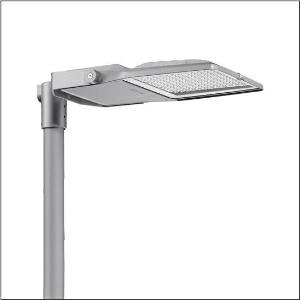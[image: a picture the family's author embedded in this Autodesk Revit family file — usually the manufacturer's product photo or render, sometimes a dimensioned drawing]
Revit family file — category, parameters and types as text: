
# Revit family: floodlight_fl_21_iq_midi___pl61_5xa7782f2c3a_b633
name_source: partatom
category: Lighting Fixtures
units: mm (PartAtom-declared; Revit-internal decimal feet)

## family parameters
Cut with Voids When Loaded = No
Host = Face
Light Source = No
Part Type = Normal
Room Calculation Point = No
Round Connector Dimension = Use Diameter
Shared = No

## types (1)
- --- (1 x LED, 35100 lm, 270.2 W, 3000K)
    Apparent Load = 270 VA
    CIE Flux Codes = 33 65 98 100 100
    Color Rendering = 70
    Color Temperature = 3000K
    Default Elevation = 1800 mm
    Description = Floodlight FL 21 iQ midi, floodlight, primary light control with lens, of PMMA, primary optical cover: protective disc, of toughened safety glass, transparent, light distribution: PL61, light emission: direct distribution, installation type: surface-mounted, lamps: LED, High Power LED, rated values: 35.100lm | 270,2W | 129,9lm/W (begin service life); end service life: 35.100lm | 286,6W; at 50% lumin. flux: 17.550lm | 117,4W | 149,5lm/W, colour temperature: 3000K, colour rendering: CRI > 70, light colour: 730, light setting 1 begin service life: 100% | 35.100lm | 270,2W | 129,9lm/W | 3.000K, light setting 1 end service life: 286,6W, further light settings possible, control: optimised constant luminous flux control (CLO 2.0), Desk-Remote (wireless, voltage-free reading and setting of iQ features in the workshop via application-optimized NFC function/RFID function), Smart-Wire, Night-Set, Temp-Guard, Auto-Match, Street-Remote, pre-setting: linear dimming characteristic, with terminal, 6-pole, mains connection: 220..240V, AC, 50/60Hz, luminaire housing, of diecast aluminium, powder-coated, SITECO metallic grey (DB 702S), corrosivity category C5 mid according to DIN EN ISO 12944suitable for swimming poolschlorine-resistant, sealing non-destructively replaceable, please order mast flange separately, mast bracket, of steel, galvanised, powder-coated, SITECO metallic grey (DB 702S), protection rating (complete): IP66, insulation class (complete): insulation class II (safety insulation), certification: CE, ENEC, VDE, protection symbol: D, impact resistance: IK08, permissible operating ambient temperature: -40..+40°C, permissible operating ambient temperature for outdoor applications: -40..+50°C, standard: DIN EN 12944, LABS conformity tested according to VDMA 24364:2018-05, packaging unit: 1 piece

Light Distribution: PL61
    Height = 76 mm
    Lamp = 1 x LED
    Lamp Light Flux = 35100 lm
    Lamp Power = 270.2 W
    Lamp count = 1
    Length = 657 mm
    Luminous efficacy = 130 lm/W
    Manufacturer = Siteco
    ModVariant = No
    Model = 5XA7782F2C3A
    Mounting Place = Pole
    Mounting Type = Pole annexe
    Number of Poles = 1
    OnlyDefault = Yes
    Power Factor = 1
    Product Name = Floodlight FL 21 iQ midi | PL61
    Product group = floodlight | pylon annexe
    ProductGroupID = 6201
    Protection Class = Protection class II
    Protection Degree = IP 66
    RLX_Detail_Level = 1
    RLX_Emergency_Light_Flux = 0 lm
    RLX_Emergency_Type = 0
    RLX_Emergency_Type_DB = No
    RlxData = <blob elided: 153953 chars, md5=d32d129d>
    Socket = socket
    Standby Power = 0 W
    System Light Flux = 35100 lm
    System Power = 270 W
    Type Comments = factory setting: luminous flux: 100 % | dim-lin: 254 | 620 mA
    Type Image = l_1007123.jpg
    URL = http://relux.com
    VarID = @adj_109799
    Voltage = 0 V
    Weight = 0.00 kg
    Width = 442 mm

## geometry (parser evidence)
native form markers: Blend x4, Sweep x15
no freeform markers — native parametric forms only
